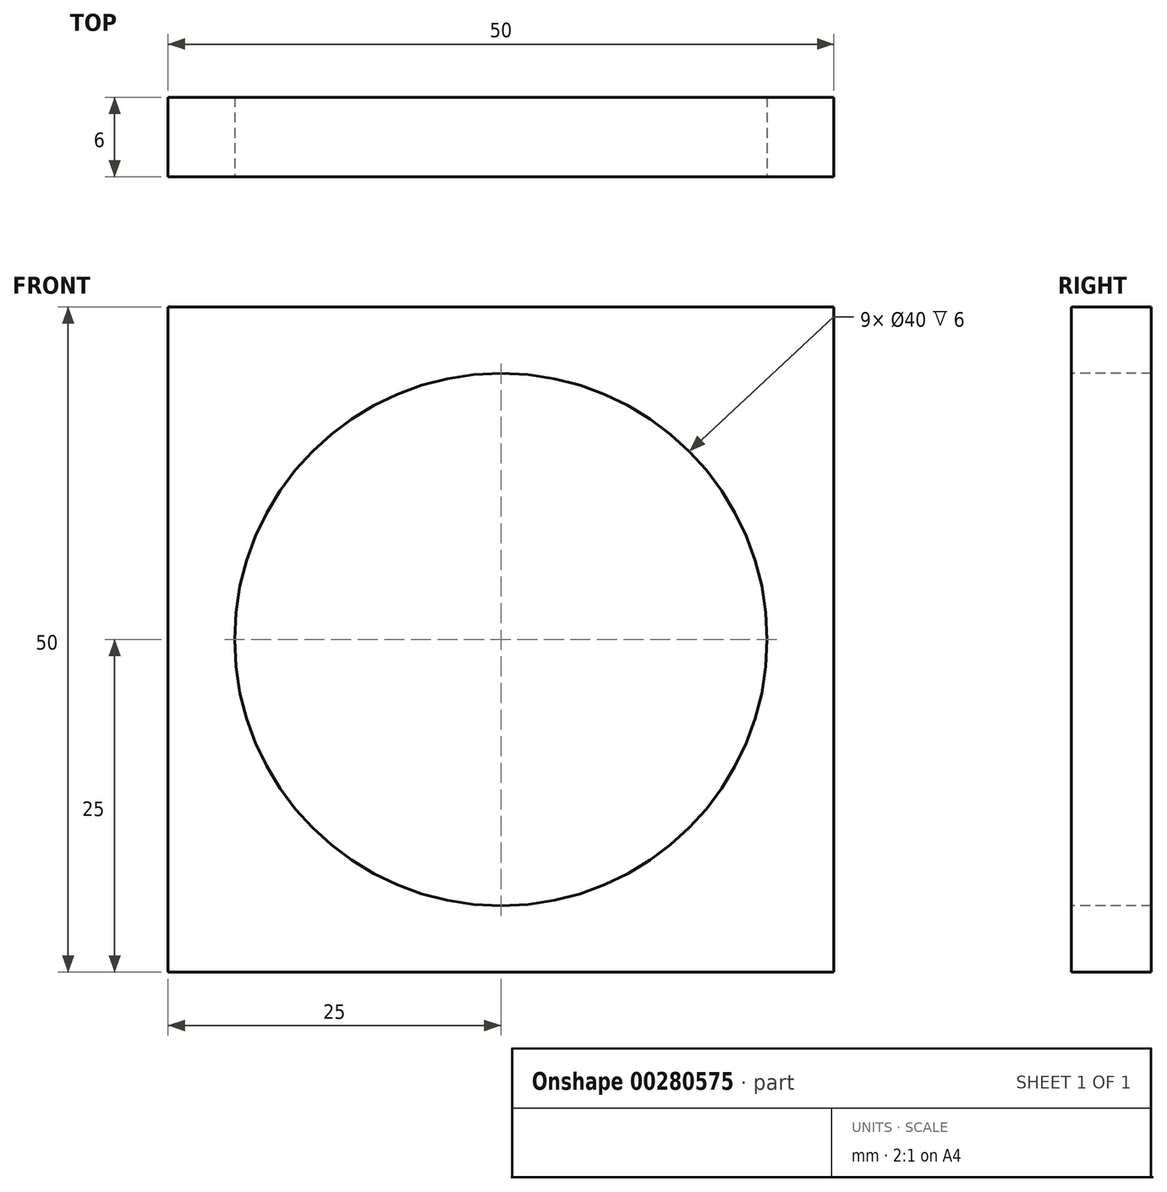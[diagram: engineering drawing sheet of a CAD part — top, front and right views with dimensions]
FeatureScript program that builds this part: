
annotation { "Feature Type Name" : "Feature", "Feature Type Description" : "" }
export const myFeature = defineFeature(function(context is Context, id is Id, definition is map)
    precondition{}
    {
        {
            var Q0;
            Q0=qCreatedBy(makeId("Top.planeOp"),FACE);
            var sketch = newSketch(context, id + "F0", { "sketchPlane" : qUnion([Q0])});
            skLineSegment(sketch, "E0.bottom", {"start": v(25, 3) * mm, "end": v(-25, 3) * mm});
            skLineSegment(sketch, "E0.top", {"start": v(25, -3) * mm, "end": v(-25, -3) * mm});
            skLineSegment(sketch, "E0.left", {"start": v(25, 3) * mm, "end": v(25, -3) * mm});
            skLineSegment(sketch, "E0.right", {"start": v(-25, 3) * mm, "end": v(-25, -3) * mm});
            skPoint(sketch, "E0.middle", {"position": v(0, 0) * mm});
            skSolve(sketch);
        }
        {
            var Q0;
            Q0 = qSketchRegion(id + "F0", true);
            extrude(context, id + "F1", {"entities" : qUnion([Q0]), "depth" : 50 * mm});
        }
        {
            var Q0;
            Q0=makeQuery(id+"F1.opExtrude","SWEPT_FACE",FACE,{"disambiguationData":[OSD([sQuery(id+"F0.wireOp",EDGE,"E0.top")])]});
            var sketch = newSketch(context, id + "F2", { "sketchPlane" : qUnion([Q0])});
            skCircle(sketch, "E1", {"center": v(0, 25) * mm, "radius": 20 * mm});
            skPoint(sketch, "E1.centerSnap0", {"position": v(-25, 25) * mm});
            skSolve(sketch);
        }
        {
            var Q0;
            Q0=makeQuery(id+"F2.imprint","IMPRINT",FACE,{"disambiguationData":[TD([[makeQuery(id+"F2.imprint","IMPRINT",EDGE,{"derivedFrom":sQuery(id+"F2.wireOp",EDGE,"E1")}),1.0]])]});
            extrude(context, id + "F3", {"entities" : qUnion([Q0]), "operationType" : NewBodyOperationType.REMOVE, "oppositeDirection" : true, "depth" : 25 * mm});
        }
    });
